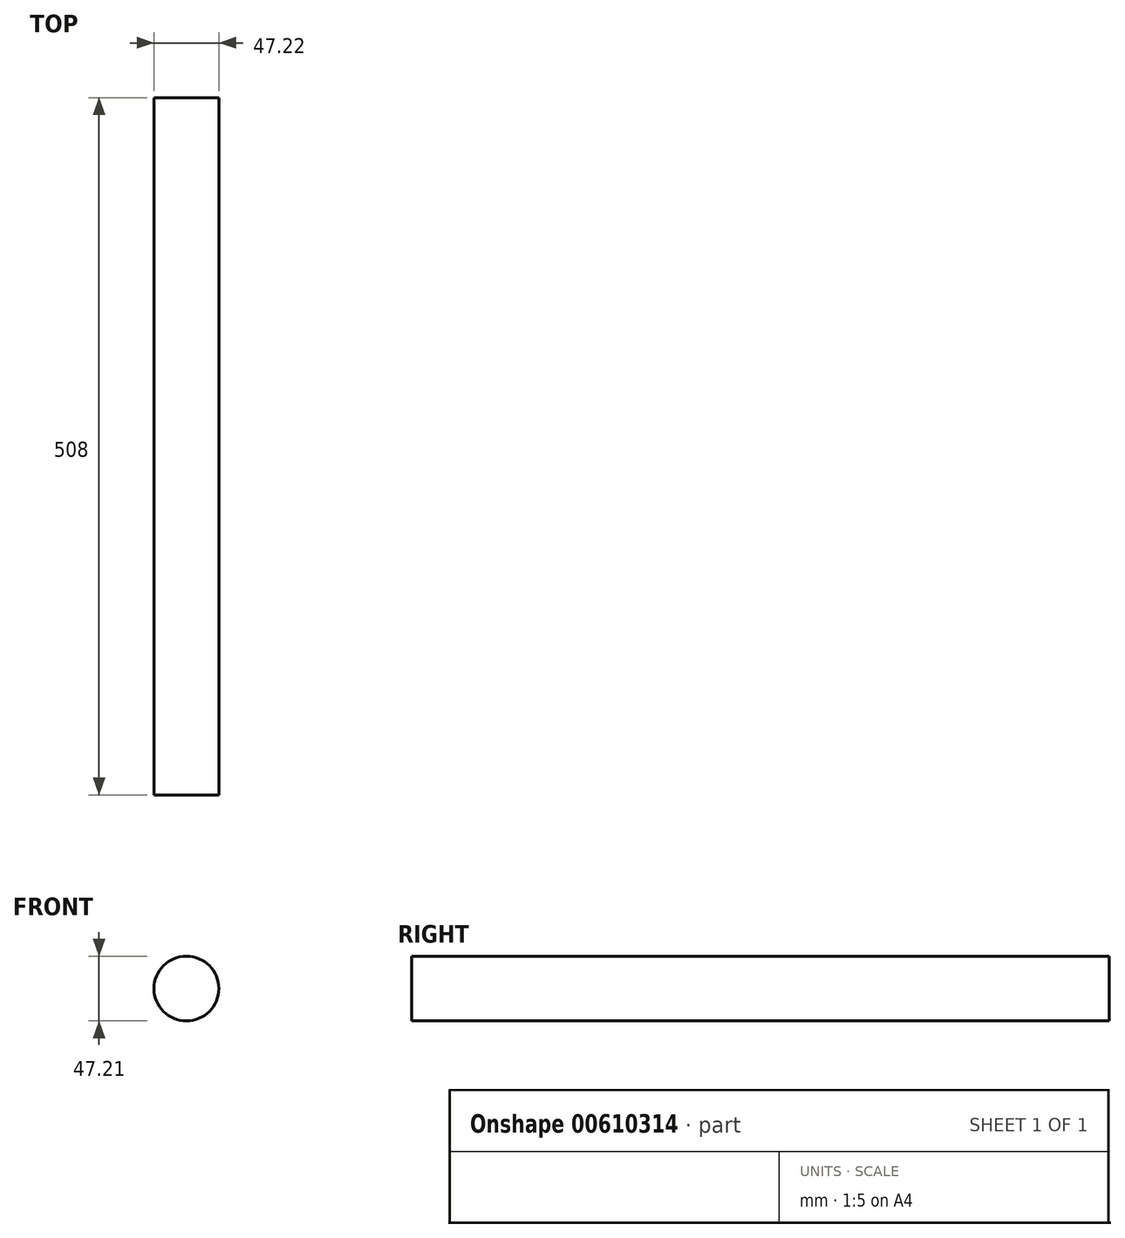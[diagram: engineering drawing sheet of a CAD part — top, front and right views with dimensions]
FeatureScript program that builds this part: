
annotation { "Feature Type Name" : "Feature", "Feature Type Description" : "" }
export const myFeature = defineFeature(function(context is Context, id is Id, definition is map)
    precondition{}
    {
        {
            var Q0;
            Q0=qCreatedBy(makeId("Front.planeOp"),FACE);
            var sketch = newSketch(context, id + "F0", { "sketchPlane" : qUnion([Q0])});
            skCircle(sketch, "E0", {"center": v(47, -39.02) * mm, "radius": 23.6 * mm});
            skCircle(sketch, "E1", {"center": v(47, -39.02) * mm, "radius": 25.4 * mm});
            skSolve(sketch);
        }
        {
            var Q0;
            Q0=makeQuery(id+"F0.imprint","IMPRINT",FACE,{"disambiguationData":[TD([[makeQuery(id+"F0.imprint","IMPRINT",EDGE,{"derivedFrom":sQuery(id+"F0.wireOp",EDGE,"E0")}),1.0]])]});
            extrude(context, id + "F1", {"entities" : qUnion([Q0]), "depth" : 508 * mm, "offsetDistance" : 25.4 * mm});
        }
    });
